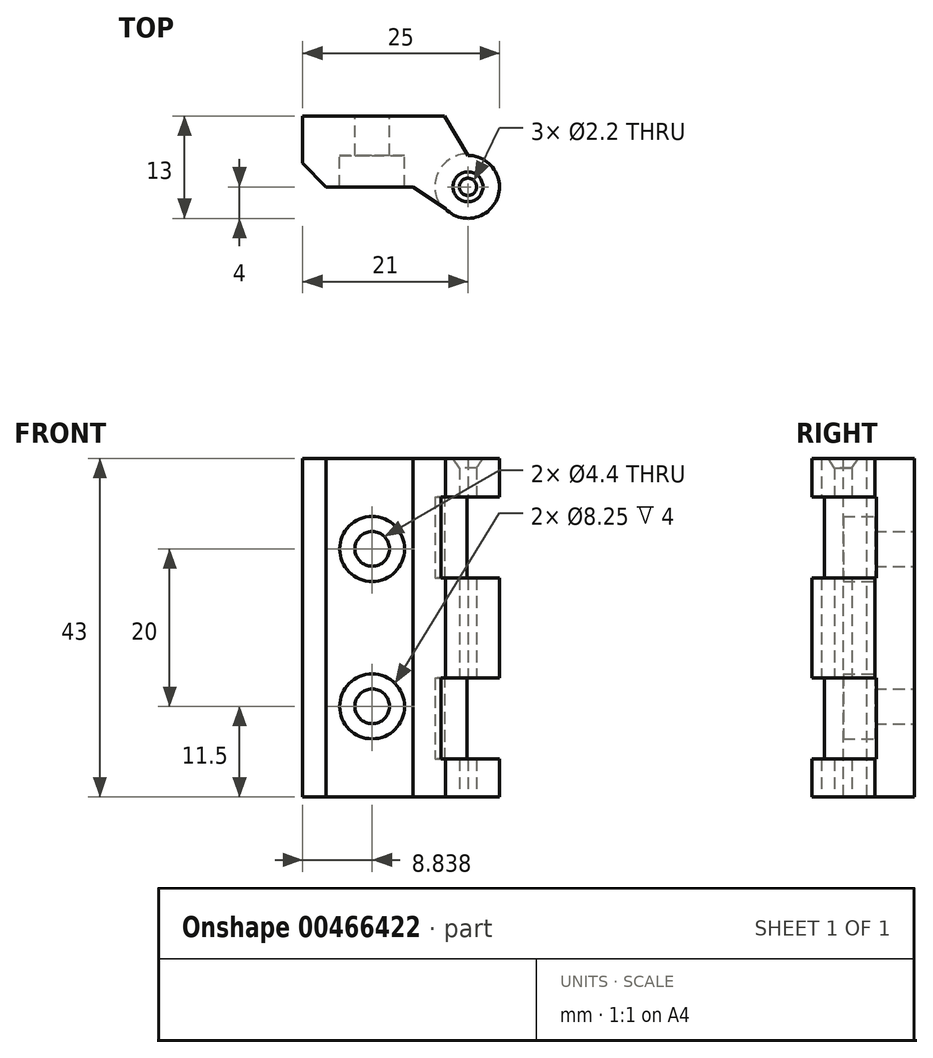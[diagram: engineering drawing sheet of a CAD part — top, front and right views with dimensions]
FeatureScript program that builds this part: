
annotation { "Feature Type Name" : "Feature", "Feature Type Description" : "" }
export const myFeature = defineFeature(function(context is Context, id is Id, definition is map)
    precondition{}
    {
        {
            var Q0;
            Q0=qCreatedBy(makeId("Top.planeOp"),FACE);
            var sketch = newSketch(context, id + "F0", { "sketchPlane" : qUnion([Q0])});
            skLineSegment(sketch, "E0.bottom", {"start": v(10.5, -4.5) * mm, "end": v(-10.5, -4.5) * mm});
            skLineSegment(sketch, "E0.top", {"start": v(10.5, 4.5) * mm, "end": v(-10.5, 4.5) * mm});
            skLineSegment(sketch, "E0.left", {"start": v(10.5, -4.5) * mm, "end": v(10.5, 4.5) * mm});
            skLineSegment(sketch, "E0.right", {"start": v(-10.5, -4.5) * mm, "end": v(-10.5, 4.5) * mm});
            skPoint(sketch, "E0.middle", {"position": v(0, 0) * mm});
            skCircle(sketch, "E1", {"center": v(10.5, -4.5) * mm, "radius": 4 * mm});
            skCircle(sketch, "E2", {"center": v(10.5, -4.5) * mm, "radius": 1.1 * mm});
            skSolve(sketch);
        }
        {
            var Q0;
            {var subQ1=sQuery(id+"F0.wireOp",EDGE,"E0.top");Q0=makeQuery(id+"F0.imprint","IMPRINT",FACE,{"disambiguationData":[TD([[makeQuery(id+"F0.imprint","IMPRINT",EDGE,{"derivedFrom":subQ1}),1.0]])]});}
            var Q1;
            {var subQ0=sQuery(id+"F0.wireOp",EDGE,"E1");var subQ1=sQuery(id+"F0.wireOp",EDGE,"E0.bottom");var subQ2=makeQuery(id+"F0.imprint","INTERSECT",VERTEX,{"derivedFrom":[subQ1,subQ0]});Q1=makeQuery(id+"F0.imprint","IMPRINT",FACE,{"disambiguationData":[TD([[makeQuery(id+"F0.imprint","IMPRINT",EDGE,{"disambiguationData":[TD([[subQ2,1.0]])],"derivedFrom":subQ1}),-1.0]])]});}
            var Q2;
            {var subQ0=sQuery(id+"F0.wireOp",EDGE,"E1");var subQ1=sQuery(id+"F0.wireOp",EDGE,"E0.bottom");var subQ2=makeQuery(id+"F0.imprint","INTERSECT",VERTEX,{"derivedFrom":[subQ1,subQ0]});Q2=makeQuery(id+"F0.imprint","IMPRINT",FACE,{"disambiguationData":[TD([[makeQuery(id+"F0.imprint","IMPRINT",EDGE,{"disambiguationData":[TD([[subQ2,1.0]])],"derivedFrom":subQ1}),1.0]])]});}
            extrude(context, id + "F1", {"entities" : qUnion([Q0, Q1, Q2]), "depth" : 43 * mm, "offsetDistance" : 25 * mm});
        }
        {
            var Q0;
            Q0=makeQuery(id+"F1.opExtrude","SWEPT_EDGE",EDGE,{"disambiguationData":[OSD([sQuery(id+"F0.wireOp",EDGE,"E0.bottom"),sQuery(id+"F0.wireOp",EDGE,"E1")])]});
            var Q1;
            Q1=makeQuery(id+"F1.opExtrude","SWEPT_EDGE",EDGE,{"disambiguationData":[OSD([sQuery(id+"F0.wireOp",EDGE,"E0.bottom"),sQuery(id+"F0.wireOp",EDGE,"E0.right")])]});
            chamfer(context, id + "F2", {"entities" : qUnion([Q0, Q1]), "width" : 3 * mm, "tangentPropagation" : true});
        }
        {
            var Q0;
            Q0=makeQuery(id+"F1.opExtrude","SWEPT_FACE",FACE,{"disambiguationData":[OSD([sQuery(id+"F0.wireOp",EDGE,"E0.bottom")])]});
            var sketch = newSketch(context, id + "F3", { "sketchPlane" : qUnion([Q0])});
            skLineSegment(sketch, "E3", {"start": v(-1.66, 43) * mm, "end": v(-1.66, 0) * mm, "construction": true});
            skPoint(sketch, "E4", {"position": v(-1.66, 11.5) * mm});
            skPoint(sketch, "E5", {"position": v(-1.66, 31.5) * mm});
            skPoint(sketch, "E6", {"position": v(-1.66, 21.5) * mm});
            skLineSegment(sketch, "E7", {"start": v(4.18, 21.5) * mm, "end": v(-7.5, 21.5) * mm, "construction": true});
            skSolve(sketch);
        }
        {
            var Q0;
            Q0=sQuery(id+"F3.wireOp",VERTEX,"E5");
            var Q1;
            Q1=sQuery(id+"F3.wireOp",VERTEX,"E4");
            var Q2;
            Q2=makeQuery(id+"F1.opExtrude","SWEPT_BODY",BODY,{"disambiguationData":[OSD([sQuery(id+"F0.wireOp",EDGE,"E0.bottom"),sQuery(id+"F0.wireOp",EDGE,"E0.top"),sQuery(id+"F0.wireOp",EDGE,"E0.left"),sQuery(id+"F0.wireOp",EDGE,"E0.right"),sQuery(id+"F0.wireOp",EDGE,"E1"),sQuery(id+"F0.wireOp",EDGE,"E2")])]});
            hole(context, id + "F4", {"style" : HoleStyle.C_BORE, "endStyle" : HoleEndStyle.THROUGH, "standardTappedOrClearance" : lookupTablePath({ "standard" : "ISO", "fit" : "Normal", "size" : "M4", "type" : "Clearance" }), "standardBlindInLast" : lookupTablePath({ "fit" : "Standard", "standard" : "ISO", "size" : "M4", "type" : "Clearance" }), "holeDiameter" : 4.4 * mm, "cBoreDiameter" : 8.25 * mm, "cBoreDepth" : 4 * mm, "majorDiameter" : 5 * mm, "isTappedThrough" : true, "tappedDepth" : 12 * mm, "tapClearance" : 3, "locations" : qUnion([Q0, Q1]), "scope" : qUnion([Q2]), "startStyle" : HoleStartStyle.PART});
        }
        {
            var Q0;
            Q0=makeQuery(id+"F1.opExtrude","SWEPT_EDGE",EDGE,{"disambiguationData":[OSD([sQuery(id+"F0.wireOp",EDGE,"E0.top"),sQuery(id+"F0.wireOp",EDGE,"E0.left")])]});
            chamfer(context, id + "F5", {"entities" : qUnion([Q0]), "chamferType" : ChamferType.TWO_OFFSETS, "width1" : 3 * mm, "oppositeDirection" : false, "width2" : 5 * mm, "tangentPropagation" : true});
        }
        {
            var Q0;
            {var subQ0=sQuery(id+"F0.wireOp",EDGE,"E0.left");var subQ1=sQuery(id+"F0.wireOp",EDGE,"E0.bottom");var subQ2=makeQuery(id+"F0.imprint","INTERSECT",VERTEX,{"derivedFrom":[subQ1,subQ0]});Q0=makeQuery(id+"F0.imprint","IMPRINT",FACE,{"disambiguationData":[TD([[makeQuery(id+"F0.imprint","IMPRINT",EDGE,{"disambiguationData":[TD([[subQ2,-1.0]])],"derivedFrom":subQ1}),1.0]])]});}
            var sketch = newSketch(context, id + "F6", { "sketchPlane" : qUnion([Q0])});
            skCircle(sketch, "E8", {"center": v(10.5, -4.5) * mm, "radius": 4.2 * mm});
            skSolve(sketch);
        }
        {
            var Q0;
            Q0 = qSketchRegion(id + "F6", true);
            extrude(context, id + "F7", {"entities" : qUnion([Q0]), "operationType" : NewBodyOperationType.REMOVE, "depth" : 15.1 * mm, "offsetDistance" : 25 * mm, "hasSecondDirection" : true, "secondDirectionOppositeDirection" : true, "secondDirectionDepth" : -4.8 * mm});
        }
        {
            var Q0;
            Q0 = qSketchRegion(id + "F6", true);
            extrude(context, id + "F8", {"entities" : qUnion([Q0]), "operationType" : NewBodyOperationType.REMOVE, "depth" : 38.1 * mm, "offsetDistance" : 25 * mm, "hasSecondDirection" : true, "secondDirectionOppositeDirection" : true, "secondDirectionDepth" : -27.8 * mm});
        }
        {
            var Q0;
            Q0=makeQuery(id+"F1.opExtrude","CAP_EDGE",EDGE,{"disambiguationData":[OSD([sQuery(id+"F0.wireOp",EDGE,"E2")])],"isStart":false});
            chamfer(context, id + "F9", {"entities" : qUnion([Q0]), "chamferType" : ChamferType.TWO_OFFSETS, "width1" : .8 * mm, "oppositeDirection" : false, "width2" : 1.2 * mm, "tangentPropagation" : true});
        }
    });
